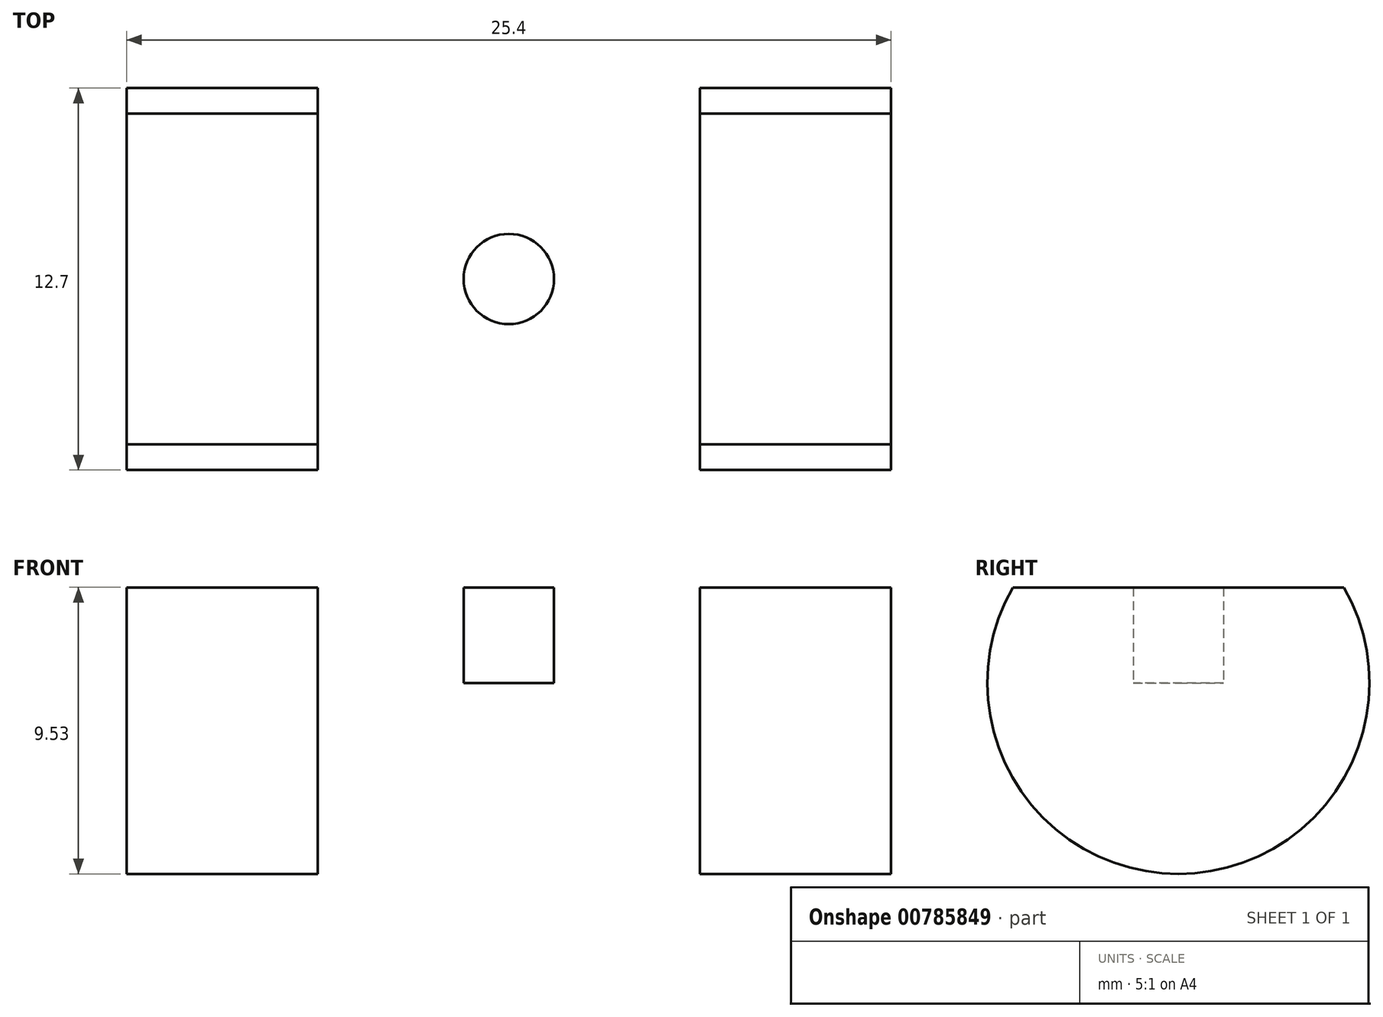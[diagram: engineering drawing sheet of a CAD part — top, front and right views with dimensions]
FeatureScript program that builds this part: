
annotation { "Feature Type Name" : "Feature", "Feature Type Description" : "" }
export const myFeature = defineFeature(function(context is Context, id is Id, definition is map)
    precondition{}
    {
        {
            var Q0;
            Q0=qCreatedBy(makeId("Right.planeOp"),FACE);
            var sketch = newSketch(context, id + "F0", { "sketchPlane" : qUnion([Q0])});
            skCircle(sketch, "E0", {"center": v(0, 0) * mm, "radius": 6.35 * mm});
            skLineSegment(sketch, "E1", {"start": v(0, 0) * mm, "end": v(0, 3.18) * mm});
            skLineSegment(sketch, "E2", {"start": v(0, 3.18) * mm, "end": v(5.5, 3.18) * mm});
            skLineSegment(sketch, "E3", {"start": v(0, 3.18) * mm, "end": v(-5.5, 3.17) * mm});
            skSolve(sketch);
        }
        {
            var Q0;
            {var subQ0=sQuery(id+"F0.wireOp",EDGE,"E2");Q0=makeQuery(id+"F0.imprint","IMPRINT",FACE,{"disambiguationData":[TD([[makeQuery(id+"F0.imprint","IMPRINT",EDGE,{"derivedFrom":subQ0}),-1.0]])]});}
            extrude(context, id + "F1", {"entities" : qUnion([Q0]), "depth" : 25.4 * mm, "offsetDistance" : 25.4 * mm});
        }
        {
            var Q0;
            Q0=qCreatedBy(makeId("Front.planeOp"),FACE);
            var sketch = newSketch(context, id + "F2", { "sketchPlane" : qUnion([Q0])});
            skLineSegment(sketch, "E4", {"start": v(0, 0) * mm, "end": v(6.35, 0) * mm});
            skLineSegment(sketch, "E5", {"start": v(6.35, 0) * mm, "end": v(6.35, -6.6) * mm});
            skLineSegment(sketch, "E6", {"start": v(6.35, -6.6) * mm, "end": v(19.05, -6.6) * mm});
            skLineSegment(sketch, "E7", {"start": v(19.05, -6.6) * mm, "end": v(19.05, 0) * mm});
            skLineSegment(sketch, "E8", {"start": v(19.05, 0) * mm, "end": v(6.35, 0) * mm});
            skSolve(sketch);
        }
        {
            var Q0;
            Q0=makeQuery(id+"F2.imprint","IMPRINT",FACE,{"disambiguationData":[TD([[makeQuery(id+"F2.imprint","IMPRINT",EDGE,{"derivedFrom":sQuery(id+"F2.wireOp",EDGE,"E5")}),1.0]])]});
            extrude(context, id + "F3", {"entities" : qUnion([Q0]), "operationType" : NewBodyOperationType.REMOVE, "oppositeDirection" : true, "depth" : 25.4 * mm, "offsetDistance" : 25.4 * mm});
        }
        {
            var Q0;
            Q0=makeQuery(id+"F3.boolean.opBoolean","COPY",FACE,{"derivedFrom":makeQuery(id+"F3.opExtrude","CAP_FACE",FACE,{"disambiguationData":[OSD([sQuery(id+"F2.wireOp",EDGE,"E5"),sQuery(id+"F2.wireOp",EDGE,"E6"),sQuery(id+"F2.wireOp",EDGE,"E7"),sQuery(id+"F2.wireOp",EDGE,"E8")])],"isStart":true})});
            extrude(context, id + "F4", {"entities" : qUnion([Q0]), "operationType" : NewBodyOperationType.REMOVE, "oppositeDirection" : true, "depth" : 25.4 * mm, "offsetDistance" : 25.4 * mm});
        }
        {
            var Q0;
            {var subQ0=sQuery(id+"F2.wireOp",EDGE,"E8");Q0=makeQuery(id+"F4.boolean.opBoolean","MERGE",FACE,{"derivedFrom":[makeQuery(id+"F3.boolean.opBoolean","COPY",FACE,{"derivedFrom":makeQuery(id+"F3.opExtrude","SWEPT_FACE",FACE,{"disambiguationData":[OSD([subQ0])]})}),makeQuery(id+"F4.opExtrude","SWEPT_FACE",FACE,{"disambiguationData":[OSD([subQ0])]})]});}
            var sketch = newSketch(context, id + "F5", { "sketchPlane" : qUnion([Q0])});
            skLineSegment(sketch, "E9", {"start": v(6.35, 0) * mm, "end": v(19.05, 0) * mm});
            skCircle(sketch, "E10", {"center": v(12.7, 0) * mm, "radius": 1.5 * mm});
            skSolve(sketch);
        }
        {
            var Q0;
            {var subQ0=sQuery(id+"F5.wireOp",EDGE,"E10");var subQ1=sQuery(id+"F5.wireOp",EDGE,"E9");var subQ2=makeQuery(id+"F5.imprint","INTERSECT",VERTEX,{"disambiguationData":[OD(0.0)],"derivedFrom":[subQ1,subQ0]});Q0=makeQuery(id+"F5.imprint","IMPRINT",FACE,{"disambiguationData":[TD([[makeQuery(id+"F5.imprint","IMPRINT",EDGE,{"disambiguationData":[TD([[subQ2,-1.0]])],"derivedFrom":subQ1}),1.0]])]});}
            var Q1;
            {var subQ0=sQuery(id+"F5.wireOp",EDGE,"E10");var subQ1=sQuery(id+"F5.wireOp",EDGE,"E9");var subQ2=makeQuery(id+"F5.imprint","INTERSECT",VERTEX,{"disambiguationData":[OD(0.0)],"derivedFrom":[subQ1,subQ0]});Q1=makeQuery(id+"F5.imprint","IMPRINT",FACE,{"disambiguationData":[TD([[makeQuery(id+"F5.imprint","IMPRINT",EDGE,{"disambiguationData":[TD([[subQ2,-1.0]])],"derivedFrom":subQ1}),-1.0]])]});}
            extrude(context, id + "F6", {"entities" : qUnion([Q0, Q1]), "operationType" : NewBodyOperationType.REMOVE, "oppositeDirection" : true, "depth" : 25.4 * mm, "offsetDistance" : 25.4 * mm});
        }
    });
